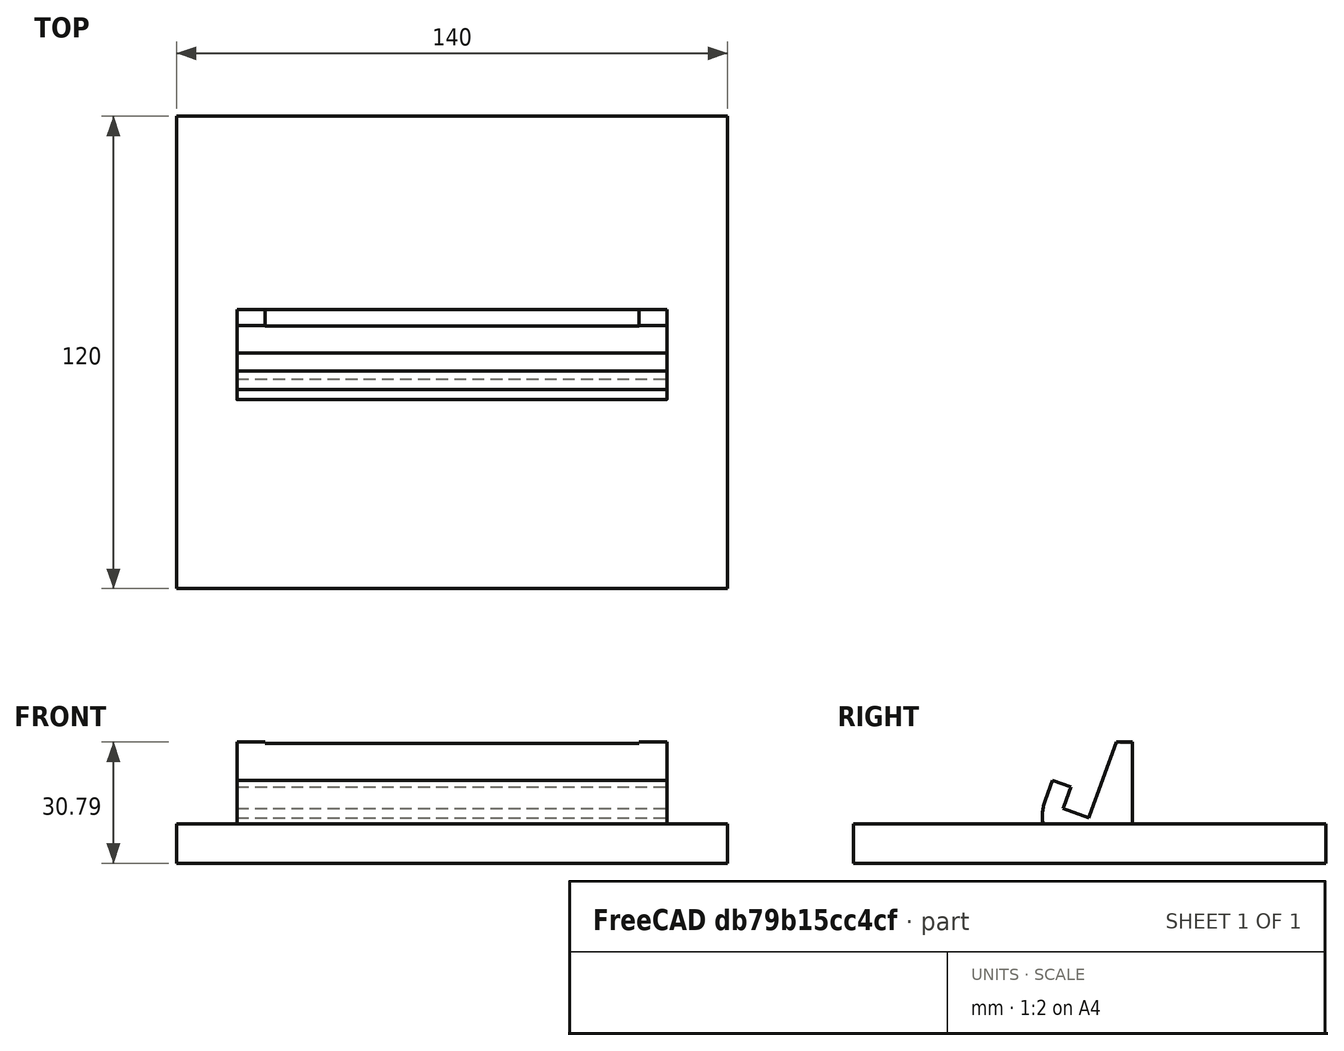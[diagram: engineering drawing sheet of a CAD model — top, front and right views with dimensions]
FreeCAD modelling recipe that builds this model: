
FCSTD DOCUMENT  (FreeCAD 1.0R39109 (Git))
Label: cradle_v2
License: All rights reserved
LicenseURL: http://en.wikipedia.org/wiki/All_rights_reserved
objects: Sketcher::SketchObject×6, Mesh::Feature×5, PartDesign::Pocket×3, PartDesign::Body×3, PartDesign::Pad×2, Spreadsheet::Sheet×1
note: 30 computed .brp shape members not serialized (recipe doc carries the construction recipe); baked Part::Feature solids carry a one-line shape summary decoded from their .brp

FEATURE [Sketcher::SketchObject] Sketch
  ArcFitTolerance = 0
  AttachmentSupport = -> [XY_Plane]
  FullyConstrained = true
  MakeInternals = false
  MapMode = 5
  sketch-geometry (4):
    g0: LineSegment StartX=-70 StartY=60 StartZ=0 EndX=70 EndY=60 EndZ=0
    g1: LineSegment StartX=70 StartY=60 StartZ=0 EndX=70 EndY=-60 EndZ=0
    g2: LineSegment StartX=70 StartY=-60 StartZ=0 EndX=-70 EndY=-60 EndZ=0
    g3: LineSegment StartX=-70 StartY=-60 StartZ=0 EndX=-70 EndY=60 EndZ=0
  constraints (10):
    c: Coincident(g0,g1)
    c: Coincident(g1,g2)
    c: Coincident(g2,g3)
    c: Coincident(g3,g0)
    c: Horizontal(g2)
    c: Vertical(g1)
    c: Symmetric(g0,g0,g-2)
    c: Symmetric(g0,g2,g-1)
    c: DistanceY(g2,g0) = 120
    c: DistanceX(g0,g0) = 140
FEATURE [PartDesign::Pad] Pad
  Direction = (0,0,1)
  Length = 10
  Length2 = 10
  Profile = -> Sketch
  ReferenceAxis = -> Sketch [N_Axis]
  Reversed = true
  Suppressed = false
  Type = 0
FEATURE [Spreadsheet::Sheet] Spreadsheet001  label="data001"
  cells = A1='tolerance; B1(tolerance)=0.25; A2='cradle_width; B2(cradle_width)=109.2; A3='cradle_height; B3(cradle_height)=20; A4='cradle_holdermag_sep; B4(cradle_holdermag_sep)=101.6; A5='cradle_holdermag_height; B5(cradle_holdermag_height)=12.7; A6='cradle_thick; B6(cradle_thick)=5; A7='cradlebase_height; B7(cradlebase_height)=7; A8='cradlebase_depth; B8(cradlebase_depth)=20; A9='cradlebase_frontdepth; B9(cradlebase_frontdepth)=10; A10='cradle_holdermag_dim1; B10(cradle_holdermag_dim1)=3; A11='cradle_holdermag_dim2; B11(cradle_holdermag_dim2)=3
FEATURE [Sketcher::SketchObject] Sketch001
  ArcFitTolerance = 0
  AttachmentSupport = -> [YZ_Plane]
  FullyConstrained = true
  MakeInternals = false
  MapMode = 5
  Placement = pos=(0,0,0) rot=(0.57735,0.57735,0.57735;2.0944rad)
  expr: Constraints[10] = <<data001>>.cradle_height
  sketch-geometry (13):
    g0: ArcOfCircle CenterX=0 CenterY=2 CenterZ=0 NormalX=0 NormalY=0 NormalZ=1 AngleXU=0 Radius=12 StartAngle=2.79253 EndAngle=4.36332
    g1: LineSegment [constr] StartX=-11.2763 StartY=6.10424 StartZ=0 EndX=0 EndY=2 EndZ=0
    g2: LineSegment StartX=0 StartY=2 StartZ=0 EndX=6.8404 EndY=20.7939 EndZ=0
    g3: LineSegment StartX=6.8404 StartY=20.7939 StartZ=0 EndX=10.8404 EndY=20.7939 EndZ=0
    g4: LineSegment StartX=10.8404 StartY=20.7939 StartZ=0 EndX=10.8404 EndY=-9.27631 EndZ=0
    g5: LineSegment StartX=-4.10424 StartY=-9.27631 StartZ=0 EndX=10.8404 EndY=-9.27631 EndZ=0
    g6: LineSegment [constr] StartX=0 StartY=2 StartZ=0 EndX=-4.10424 EndY=-9.27631 EndZ=0
    g7: LineSegment StartX=0 StartY=2 StartZ=0 EndX=-0.17101 EndY=1.53015 EndZ=0
    g8: LineSegment StartX=-0.17101 StartY=1.53015 StartZ=0 EndX=-6.74886 EndY=3.92429 EndZ=0
    g9: LineSegment StartX=-6.74886 StartY=3.92429 StartZ=0 EndX=-6.57785 EndY=4.39414 EndZ=0
    g10: LineSegment StartX=-11.2763 StartY=6.10424 StartZ=0 EndX=-9.45646 EndY=11.1042 EndZ=0
    g11: LineSegment StartX=-9.45646 StartY=11.1042 StartZ=0 EndX=-4.758 EndY=9.39414 EndZ=0
    g12: LineSegment StartX=-4.758 StartY=9.39414 StartZ=0 EndX=-6.57785 EndY=4.39414 EndZ=0
  constraints (37):
    c: Radius(g0) = 12
    c: Coincident(g1,g0)
    c: Coincident(g1,g0)
    c: Coincident(g2,g0)
    c: Coincident(g3,g2)
    c: Horizontal(g3)
    c: Coincident(g5,g0)
    c: Coincident(g5,g4)
    c: Horizontal(g5)
    c: Vertical(g4)
    c: Distance(g2,g0) = 20
    c: Distance(g0,g-1) = 2
    c: Coincident(g4,g3)
    c: PointOnObject(g0,g-2)
    c: Coincident(g6,g0)
    c: Coincident(g6,g0)
    c: Angle(g1,g6) = 1.5708
    c: Angle(g2,g1) = 1.5708
    c: DistanceX(g2,g3) = 4
    c: Angle(g6,g-2) = 0.349066  'tilt angle'
    c: Coincident(g7,g0)
    c: PointOnObject(g7,g6)
    c: Coincident(g8,g7)
    c: Coincident(g9,g8)
    c: PointOnObject(g9,g1)
    c: Distance(g7,g0) = 0.5
    c: Distance(g8,g7) = 7
    c: Parallel(g9,g6)
    c: Parallel(g8,g1)
    c: Coincident(g10,g0)
    c: Coincident(g11,g10)
    c: Parallel(g11,g1)
    c: Parallel(g10,g2)
    c: Coincident(g12,g11)
    c: Coincident(g12,g9)
    c: Parallel(g10,g12)
    c: DistanceY(g0,g10) = 5
FEATURE [PartDesign::Pad] Pad001
  BaseFeature = -> Pad
  Direction = (1,0,0)
  Length = 109.2
  Length2 = 10
  Midplane = true
  Profile = -> Sketch001
  ReferenceAxis = -> Sketch001 [N_Axis]
  Suppressed = false
  Type = 0
  expr: Length = <<data001>>.cradle_width
FEATURE [Sketcher::SketchObject] Sketch002
  ArcFitTolerance = 0
  AttachmentSupport = -> [Pad001]
  FullyConstrained = true
  MakeInternals = false
  MapMode = 5
  Placement = pos=(0,0,20.7939) rot=(0,0,1;0rad)
  expr: Constraints[10] = 24
  expr: Constraints[8] = 95
  sketch-geometry (4):
    g0: LineSegment StartX=-47.5 StartY=24 StartZ=0 EndX=47.5 EndY=24 EndZ=0
    g1: LineSegment StartX=47.5 StartY=24 StartZ=0 EndX=47.5 EndY=0 EndZ=0
    g2: LineSegment StartX=47.5 StartY=0 StartZ=0 EndX=-47.5 EndY=0 EndZ=0
    g3: LineSegment StartX=-47.5 StartY=0 StartZ=0 EndX=-47.5 EndY=24 EndZ=0
  constraints (11):
    c: Coincident(g0,g1)
    c: Coincident(g1,g2)
    c: Coincident(g2,g3)
    c: Coincident(g3,g0)
    c: Horizontal(g2)
    c: Vertical(g1)
    c: Vertical(g3)
    c: PointOnObject(g1,g-1)
    c: DistanceX(g0,g0) = 95
    c: Symmetric(g0,g0,g-2)
    c: DistanceY(g2,g0) = 24
FEATURE [PartDesign::Pocket] Pocket
  BaseFeature = -> Pad001
  Direction = (0,0,-1)
  Length = 0.3
  Length2 = 5
  Profile = -> Sketch002
  ReferenceAxis = -> Sketch002 [N_Axis]
  Suppressed = false
  Type = 0
FEATURE [Sketcher::SketchObject] Sketch003
  ArcFitTolerance = 0
  AttachmentSupport = -> [Pocket]
  FullyConstrained = true
  MakeInternals = false
  MapMode = 5
  Placement = pos=(0,0,20.7939) rot=(0,0,1;0rad)
  sketch-geometry (1):
    g0: Circle CenterX=-50.8 CenterY=12.7 CenterZ=0 NormalX=0 NormalY=0 NormalZ=1 AngleXU=0 Radius=1.75
  constraints (3):
    c: DistanceX(g0,g-1) = 50.8
    c: DistanceY(g-1,g0) = 12.7
    c: Radius(g0) = 1.75
FEATURE [PartDesign::Pocket] Pocket001
  BaseFeature = -> Pocket
  Direction = (0,0,-1)
  Length = 3.25
  Length2 = 5
  Profile = -> Sketch003
  ReferenceAxis = -> Sketch003 [N_Axis]
  Suppressed = false
  Type = 0
FEATURE [Sketcher::SketchObject] Sketch004
  ArcFitTolerance = 0
  AttachmentSupport = -> [Pocket001]
  FullyConstrained = true
  MakeInternals = false
  MapMode = 5
  Placement = pos=(0,0,20.7939) rot=(0,0,1;0rad)
  sketch-geometry (1):
    g0: Circle CenterX=50.8 CenterY=12.7 CenterZ=0 NormalX=0 NormalY=0 NormalZ=1 AngleXU=0 Radius=1.75
  constraints (3):
    c: DistanceX(g-1,g0) = 50.8
    c: DistanceY(g-1,g0) = 12.7
    c: Radius(g0) = 1.75
FEATURE [PartDesign::Pocket] Pocket002
  BaseFeature = -> Pocket001
  Direction = (0,0,-1)
  Length = 3.25
  Length2 = 5
  Profile = -> Sketch004
  ReferenceAxis = -> Sketch004 [N_Axis]
  Suppressed = false
  Type = 0
FEATURE [PartDesign::Body] Body
  AllowCompound = false
  Group = -> [Sketch,Pad,Sketch001,Pad001,Sketch002,Pocket,Sketch003,Pocket001,Sketch004,Pocket002]
  Origin = -> Origin
  Tip = -> Pocket002
FEATURE [Mesh::Feature] Mesh  label="20 degrees"
FEATURE [Mesh::Feature] Mesh001  label="30 degrees"
FEATURE [Mesh::Feature] Mesh002  label="5 degrees"
FEATURE [Mesh::Feature] Mesh003  label="0 degrees"
FEATURE [Mesh::Feature] Mesh004  label="Body (Meshed)"
FEATURE [Sketcher::SketchObject] Sketch005
  ArcFitTolerance = 1e-06
  AttachmentSupport = -> [XY_Plane001]
  FullyConstrained = true
  MakeInternals = false
  MapMode = 5
FEATURE [PartDesign::Body] Body001
  AllowCompound = false
  Group = -> [Sketch005]
  Origin = -> Origin001
FEATURE [PartDesign::Body] Body002
  AllowCompound = false
  Origin = -> Origin002
